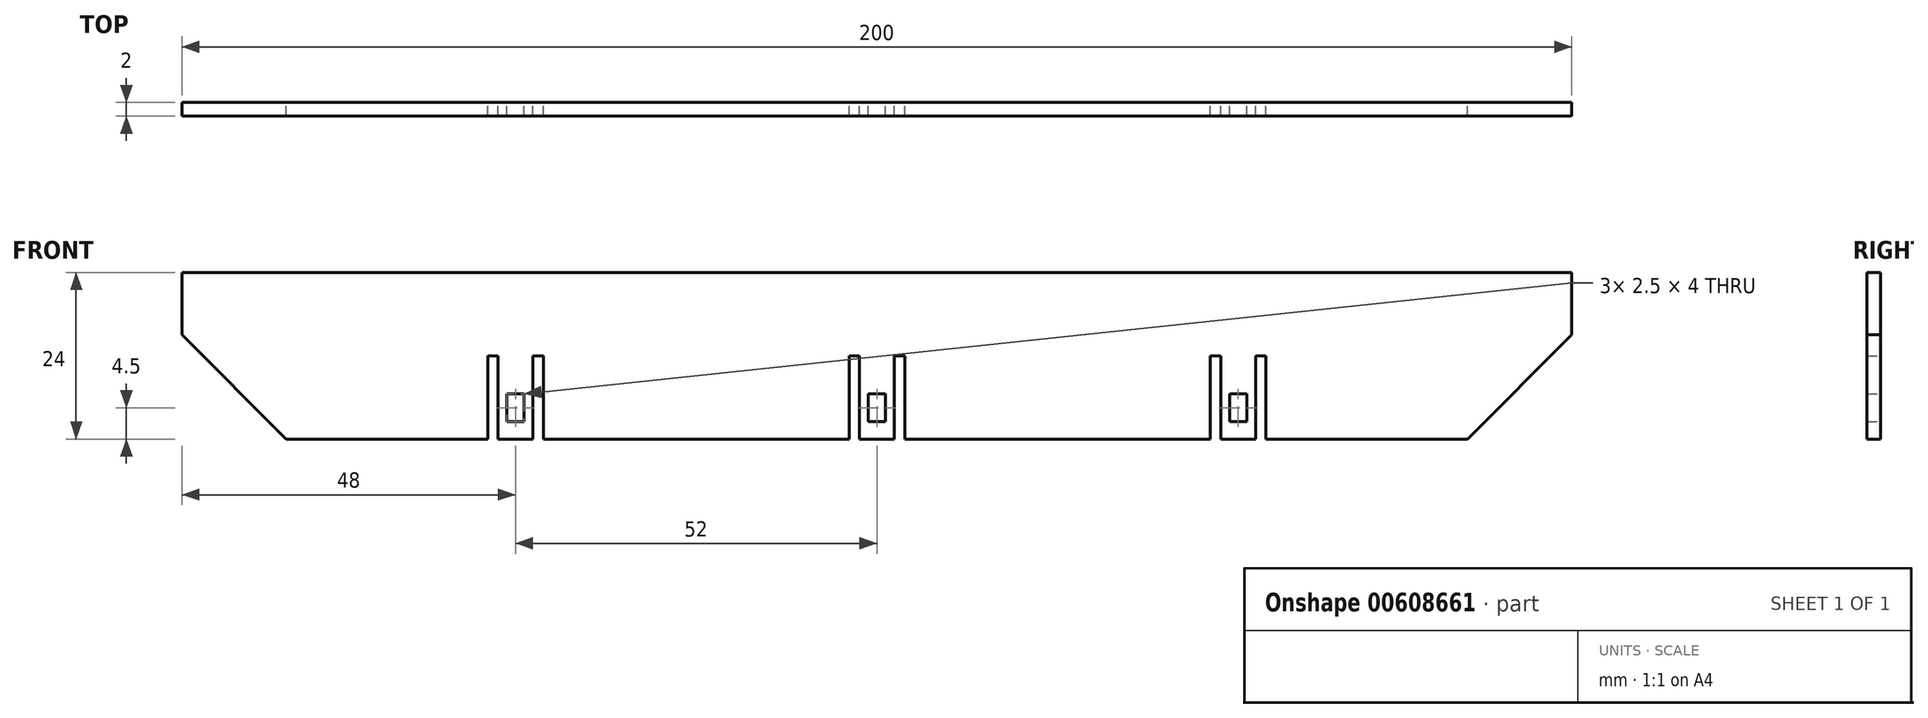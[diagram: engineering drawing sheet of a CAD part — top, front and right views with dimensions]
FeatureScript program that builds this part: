
annotation { "Feature Type Name" : "Feature", "Feature Type Description" : "" }
export const myFeature = defineFeature(function(context is Context, id is Id, definition is map)
    precondition{}
    {
        {
            var Q0;
            Q0=qCreatedBy(makeId("Front.planeOp"),FACE);
            var sketch = newSketch(context, id + "F0", { "sketchPlane" : qUnion([Q0])});
            skLineSegment(sketch, "E0.bottom", {"start": v(85, -7.5) * mm, "end": v(-85, -7.5) * mm});
            skLineSegment(sketch, "E0.top", {"start": v(85, 7.5) * mm, "end": v(-85, 7.5) * mm});
            skLineSegment(sketch, "E0.left", {"start": v(85, -7.5) * mm, "end": v(85, 7.5) * mm});
            skLineSegment(sketch, "E0.right", {"start": v(-85, -7.5) * mm, "end": v(-85, 7.5) * mm});
            skPoint(sketch, "E0.middle", {"position": v(0, 0) * mm});
            skLineSegment(sketch, "E1.bottom", {"start": v(-85, -7.5) * mm, "end": v(-100, -7.5) * mm});
            skLineSegment(sketch, "E1.top", {"start": v(-85, 7.5) * mm, "end": v(-100, 7.5) * mm});
            skLineSegment(sketch, "E1.right", {"start": v(-100, -7.5) * mm, "end": v(-100, 7.5) * mm});
            skPoint(sketch, "E1.middle", {"position": v(-92.5, 0) * mm});
            skLineSegment(sketch, "E2", {"start": v(-100, 7.5) * mm, "end": v(-85, -7.5) * mm});
            skLineSegment(sketch, "E3.bottom", {"start": v(100, -7.5) * mm, "end": v(85, -7.5) * mm});
            skLineSegment(sketch, "E3.top", {"start": v(100, 7.5) * mm, "end": v(85, 7.5) * mm});
            skLineSegment(sketch, "E3.left", {"start": v(100, -7.5) * mm, "end": v(100, 7.5) * mm});
            skPoint(sketch, "E3.middle", {"position": v(92.5, 0) * mm});
            skLineSegment(sketch, "E4", {"start": v(85, -7.5) * mm, "end": v(100, 7.5) * mm});
            skLineSegment(sketch, "E5.bottom", {"start": v(-54.5, -7.5) * mm, "end": v(-56, -7.5) * mm});
            skLineSegment(sketch, "E5.top", {"start": v(-54.5, 4.5) * mm, "end": v(-56, 4.5) * mm});
            skLineSegment(sketch, "E5.left", {"start": v(-54.5, -7.5) * mm, "end": v(-54.5, 4.5) * mm});
            skLineSegment(sketch, "E5.right", {"start": v(-56, -7.5) * mm, "end": v(-56, 4.5) * mm});
            skPoint(sketch, "E5.middle", {"position": v(-55.25, -1.5) * mm});
            skLineSegment(sketch, "E6.bottom", {"start": v(-48, -7.5) * mm, "end": v(-49.5, -7.5) * mm});
            skLineSegment(sketch, "E6.top", {"start": v(-48, 4.5) * mm, "end": v(-49.5, 4.5) * mm});
            skLineSegment(sketch, "E6.left", {"start": v(-48, -7.5) * mm, "end": v(-48, 4.5) * mm});
            skLineSegment(sketch, "E6.right", {"start": v(-49.5, -7.5) * mm, "end": v(-49.5, 4.5) * mm});
            skPoint(sketch, "E6.middle", {"position": v(-48.75, -1.5) * mm});
            skLineSegment(sketch, "E7.bottom", {"start": v(-2.5, -7.5) * mm, "end": v(-4, -7.5) * mm});
            skLineSegment(sketch, "E7.top", {"start": v(-2.5, 4.5) * mm, "end": v(-4, 4.5) * mm});
            skLineSegment(sketch, "E7.left", {"start": v(-2.5, -7.5) * mm, "end": v(-2.5, 4.5) * mm});
            skLineSegment(sketch, "E7.right", {"start": v(-4, -7.5) * mm, "end": v(-4, 4.5) * mm});
            skPoint(sketch, "E7.middle", {"position": v(-3.25, -1.5) * mm});
            skLineSegment(sketch, "E8.bottom", {"start": v(4, -7.5) * mm, "end": v(2.5, -7.5) * mm});
            skLineSegment(sketch, "E8.top", {"start": v(4, 4.5) * mm, "end": v(2.5, 4.5) * mm});
            skLineSegment(sketch, "E8.left", {"start": v(4, -7.5) * mm, "end": v(4, 4.5) * mm});
            skLineSegment(sketch, "E8.right", {"start": v(2.5, -7.5) * mm, "end": v(2.5, 4.5) * mm});
            skPoint(sketch, "E8.middle", {"position": v(3.25, -1.5) * mm});
            skLineSegment(sketch, "E9.bottom", {"start": v(49.5, -7.5) * mm, "end": v(48, -7.5) * mm});
            skLineSegment(sketch, "E9.top", {"start": v(49.5, 4.5) * mm, "end": v(48, 4.5) * mm});
            skLineSegment(sketch, "E9.left", {"start": v(49.5, -7.5) * mm, "end": v(49.5, 4.5) * mm});
            skLineSegment(sketch, "E9.right", {"start": v(48, -7.5) * mm, "end": v(48, 4.5) * mm});
            skPoint(sketch, "E9.middle", {"position": v(48.75, -1.5) * mm});
            skLineSegment(sketch, "E10.bottom", {"start": v(56, -7.5) * mm, "end": v(54.5, -7.5) * mm});
            skLineSegment(sketch, "E10.top", {"start": v(56, 4.5) * mm, "end": v(54.5, 4.5) * mm});
            skLineSegment(sketch, "E10.left", {"start": v(56, -7.5) * mm, "end": v(56, 4.5) * mm});
            skLineSegment(sketch, "E10.right", {"start": v(54.5, -7.5) * mm, "end": v(54.5, 4.5) * mm});
            skPoint(sketch, "E10.middle", {"position": v(55.25, -1.5) * mm});
            skLineSegment(sketch, "E11.bottom", {"start": v(-50.75, -5) * mm, "end": v(-53.25, -5) * mm});
            skLineSegment(sketch, "E11.top", {"start": v(-50.75, -1) * mm, "end": v(-53.25, -1) * mm});
            skLineSegment(sketch, "E11.left", {"start": v(-50.75, -5) * mm, "end": v(-50.75, -1) * mm});
            skLineSegment(sketch, "E11.right", {"start": v(-53.25, -5) * mm, "end": v(-53.25, -1) * mm});
            skPoint(sketch, "E11.middle", {"position": v(-52, -3) * mm});
            skLineSegment(sketch, "E12.bottom", {"start": v(53.25, -5) * mm, "end": v(50.75, -5) * mm});
            skLineSegment(sketch, "E12.top", {"start": v(53.25, -1) * mm, "end": v(50.75, -1) * mm});
            skLineSegment(sketch, "E12.left", {"start": v(53.25, -5) * mm, "end": v(53.25, -1) * mm});
            skLineSegment(sketch, "E12.right", {"start": v(50.75, -5) * mm, "end": v(50.75, -1) * mm});
            skPoint(sketch, "E12.middle", {"position": v(52, -3) * mm});
            skLineSegment(sketch, "E13.bottom", {"start": v(1.25, -5) * mm, "end": v(-1.25, -5) * mm});
            skLineSegment(sketch, "E13.top", {"start": v(1.25, -1) * mm, "end": v(-1.25, -1) * mm});
            skLineSegment(sketch, "E13.left", {"start": v(1.25, -5) * mm, "end": v(1.25, -1) * mm});
            skLineSegment(sketch, "E13.right", {"start": v(-1.25, -5) * mm, "end": v(-1.25, -1) * mm});
            skPoint(sketch, "E13.middle", {"position": v(0, -3) * mm});
            skLineSegment(sketch, "E14.bottom", {"start": v(100, 7.5) * mm, "end": v(-100, 7.5) * mm});
            skLineSegment(sketch, "E14.top", {"start": v(100, 16.5) * mm, "end": v(-100, 16.5) * mm});
            skLineSegment(sketch, "E14.left", {"start": v(100, 7.5) * mm, "end": v(100, 16.5) * mm});
            skLineSegment(sketch, "E14.right", {"start": v(-100, 7.5) * mm, "end": v(-100, 16.5) * mm});
            skPoint(sketch, "E14.middle", {"position": v(0, 12) * mm});
            skSolve(sketch);
        }
        {
            var Q0;
            Q0=makeQuery(id+"F0.imprint","IMPRINT",FACE,{"disambiguationData":[TD([[makeQuery(id+"F0.imprint","IMPRINT",EDGE,{"derivedFrom":sQuery(id+"F0.wireOp",EDGE,"E0.bottom")}),-1.0]])]});
            var Q1;
            Q1=makeQuery(id+"F0.imprint","IMPRINT",FACE,{"disambiguationData":[TD([[makeQuery(id+"F0.imprint","IMPRINT",EDGE,{"derivedFrom":sQuery(id+"F0.wireOp",EDGE,"E1.top")}),1.0]])]});
            var Q2;
            Q2=makeQuery(id+"F0.imprint","IMPRINT",FACE,{"disambiguationData":[TD([[makeQuery(id+"F0.imprint","IMPRINT",EDGE,{"derivedFrom":sQuery(id+"F0.wireOp",EDGE,"E3.top")}),1.0]])]});
            var Q3;
            Q3=makeQuery(id+"F0.imprint","IMPRINT",FACE,{"disambiguationData":[TD([[makeQuery(id+"F0.imprint","IMPRINT",EDGE,{"derivedFrom":sQuery(id+"F0.wireOp",EDGE,"OD9o5IjV-5K3p-bvsU-E8e2-8qKfq0g9wVGw.bottom")}),-1.0]])]});
            var Q4;
            {var subQ0=sQuery(id+"F0.wireOp",EDGE,"E0.right");Q4=makeQuery(id+"F0.imprint","IMPRINT",FACE,{"disambiguationData":[TD([[makeQuery(id+"F0.imprint","IMPRINT",EDGE,{"derivedFrom":subQ0}),1.0]])]});}
            var Q5;
            Q5=makeQuery(id+"F0.imprint","IMPRINT",FACE,{"disambiguationData":[TD([[makeQuery(id+"F0.imprint","IMPRINT",EDGE,{"derivedFrom":sQuery(id+"F0.wireOp",EDGE,"E14.top")}),1.0]])]});
            var Q6;
            {var subQ0=sQuery(id+"F0.wireOp",EDGE,"E0.left");Q6=makeQuery(id+"F0.imprint","IMPRINT",FACE,{"disambiguationData":[TD([[makeQuery(id+"F0.imprint","IMPRINT",EDGE,{"derivedFrom":subQ0}),-1.0]])]});}
            extrude(context, id + "F1", {"entities" : qUnion([Q0, Q1, Q2, Q3, Q4, Q5, Q6]), "depth" : 2 * mm, "offsetDistance" : 25 * mm});
        }
    });
